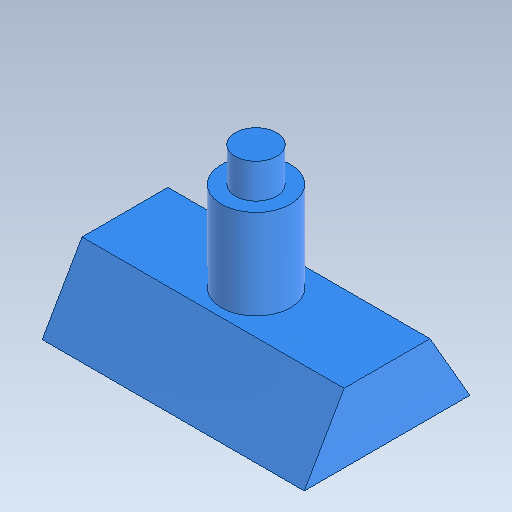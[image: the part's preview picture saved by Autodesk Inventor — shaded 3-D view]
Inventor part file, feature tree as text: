
AUTODESK INVENTOR PART (.ipt)
format: ipt  version: 2020.5 (Build 245400000, 400)  size: 100,864 bytes
history: native  units: mm
features: extrude x3, sketch x3
ambient origin geometry x8: Origin, YZ Plane, XZ Plane, XY Plane, X Axis, Y Axis, Z Axis, Center Point
bodies: Body1 (feature_tree)
feature tree (6):
  extrude  "Extrusion3"  TaperAngle=60.0deg  [1 undecoded]
  extrude  "Extrusion4"  Depth=12.0mm
  extrude  "Extrusion5"  Depth=10.0mm
  sketch  "Sketch4"  dims[d31=60.0deg d32=60.0deg]
  sketch  "Sketch5"  dims[d33=10.0mm d34=12.0mm]
  sketch  "Sketch6"  dims[d35=38.0mm d36=0.0mm d37=10.0mm d38=13.0mm d39=0.0mm d40=6.0mm d41=5.0mm d42=0.0mm]
note: 1 required parameter value undecoded (feature->parameter linkage not recoverable at this tier; creation-order binding heuristic only, values carry confidence <= 0.55)
